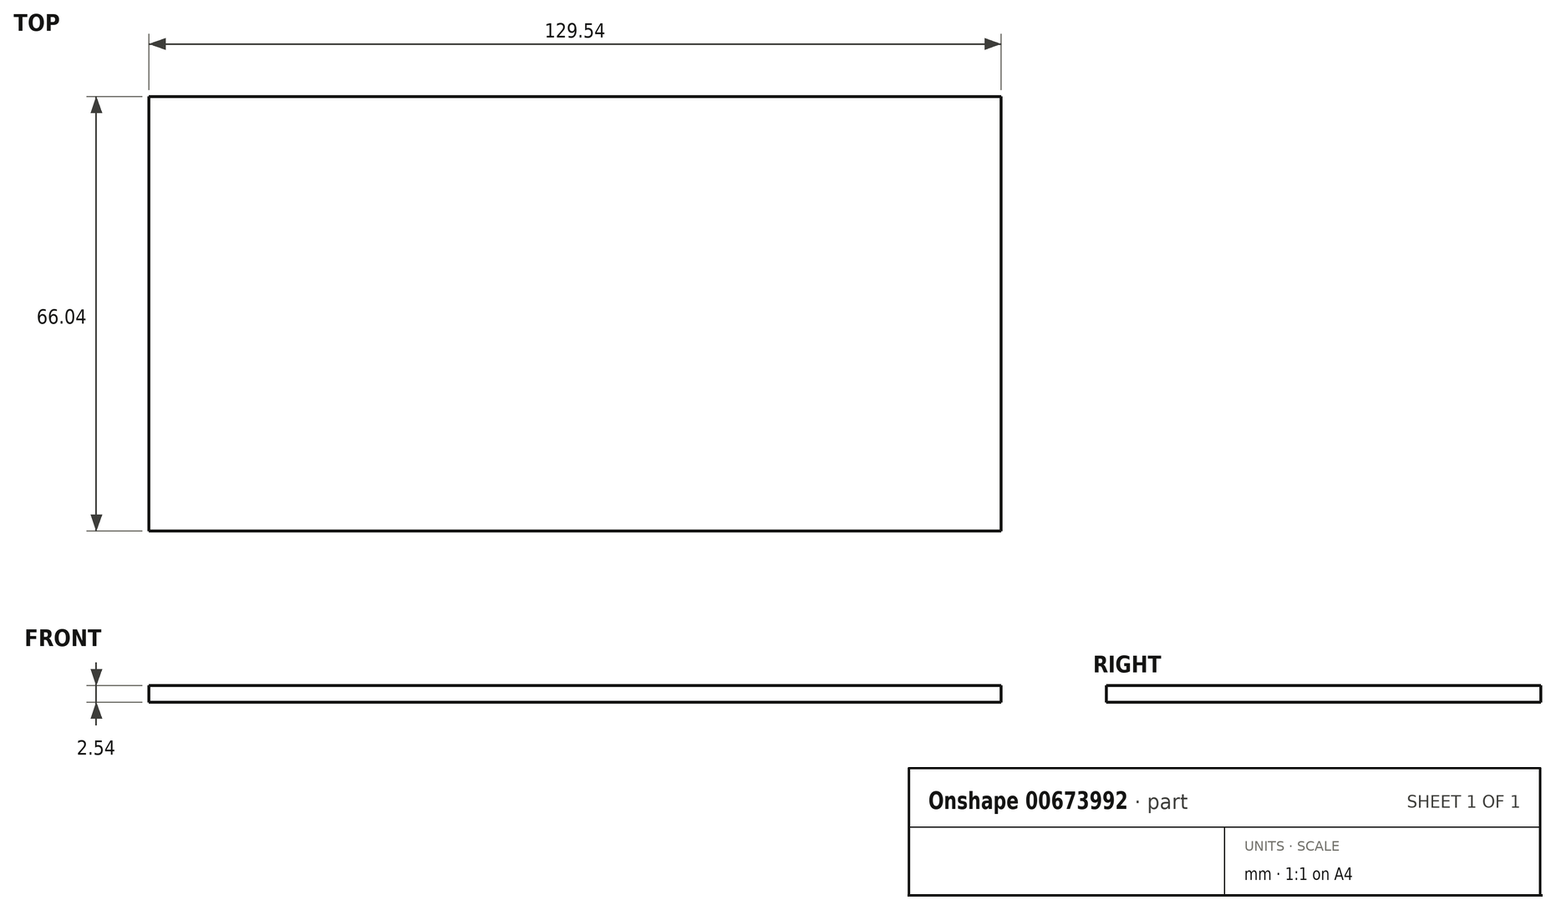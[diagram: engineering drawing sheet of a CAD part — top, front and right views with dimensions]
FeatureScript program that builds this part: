
annotation { "Feature Type Name" : "Feature", "Feature Type Description" : "" }
export const myFeature = defineFeature(function(context is Context, id is Id, definition is map)
    precondition{}
    {
        {
            var Q0;
            Q0=qCreatedBy(makeId("Front.planeOp"),FACE);
            var sketch = newSketch(context, id + "F0", { "sketchPlane" : qUnion([Q0])});
            skLineSegment(sketch, "E0", {"start": v(5.08, 12.7) * mm, "end": v(134.62, 12.7) * mm});
            skLineSegment(sketch, "E1", {"start": v(5.08, 12.7) * mm, "end": v(5.08, 10.16) * mm});
            skLineSegment(sketch, "E2", {"start": v(5.08, 10.16) * mm, "end": v(134.62, 10.16) * mm});
            skLineSegment(sketch, "E3", {"start": v(134.62, 10.16) * mm, "end": v(134.62, 12.7) * mm});
            skSolve(sketch);
        }
        {
            var Q0;
            Q0 = qSketchRegion(id + "F0", true);
            extrude(context, id + "F1", {"entities" : qUnion([Q0]), "depth" : 66.04 * mm, "offsetDistance" : 25.4 * mm});
        }
    });
